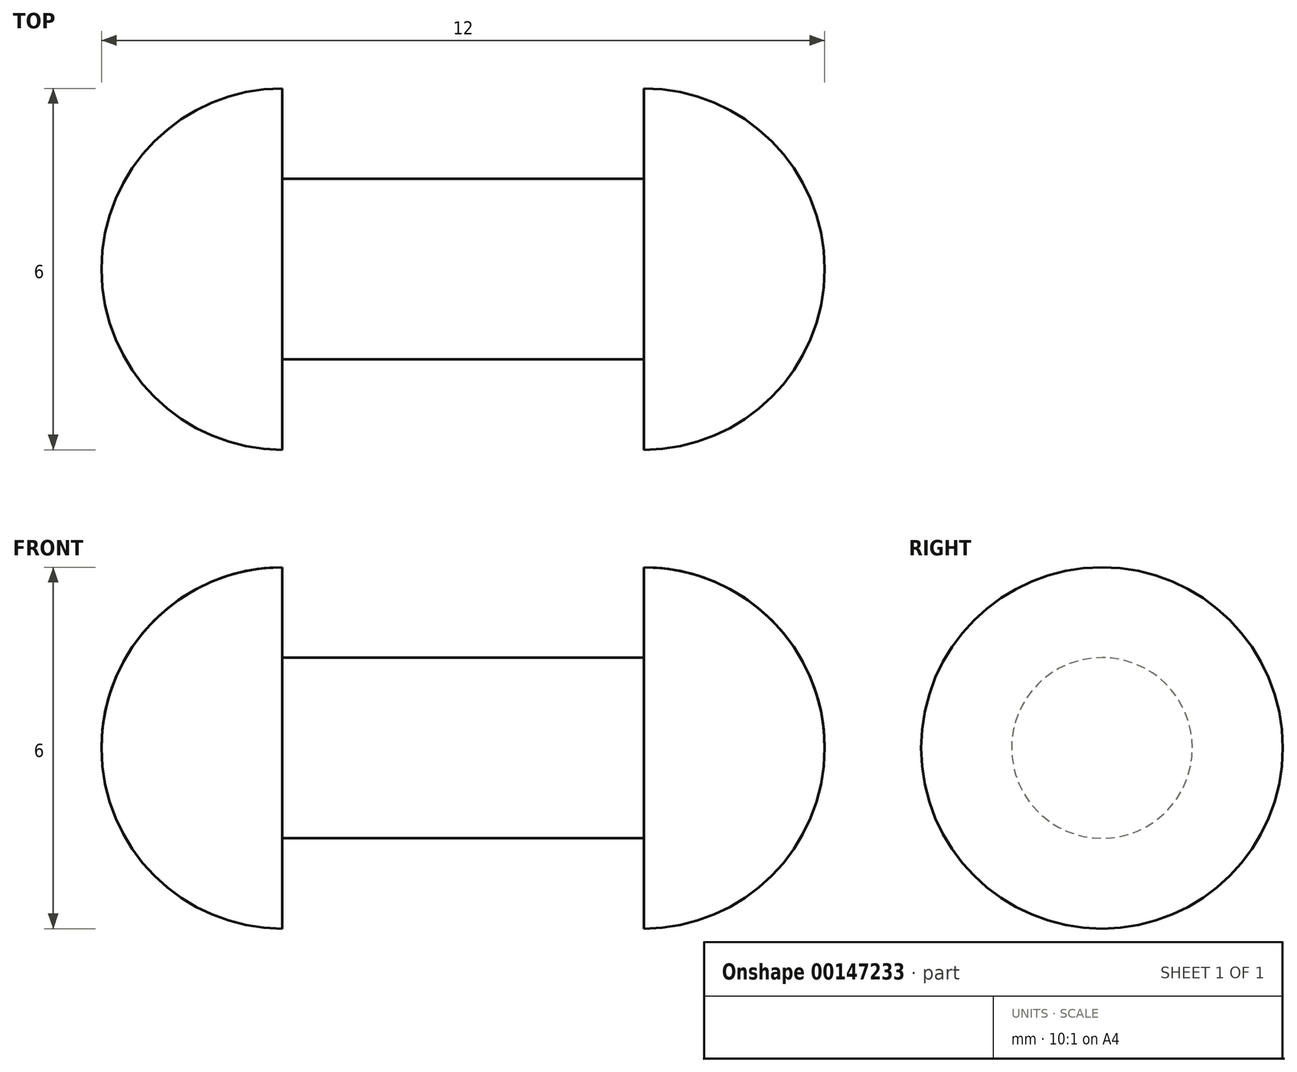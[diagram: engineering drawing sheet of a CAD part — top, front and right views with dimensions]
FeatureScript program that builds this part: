
annotation { "Feature Type Name" : "Feature", "Feature Type Description" : "" }
export const myFeature = defineFeature(function(context is Context, id is Id, definition is map)
    precondition{}
    {
        {
            var Q0;
            Q0=qCreatedBy(makeId("Front.planeOp"),FACE);
            var sketch = newSketch(context, id + "F0", { "sketchPlane" : qUnion([Q0])});
            skArc(sketch, "E0", {"start": v(0, 3) * mm, "mid": v(-2.12, 2.12) * mm, "end": v(-3, 0) * mm});
            skArc(sketch, "E1", {"start": v(9, 0) * mm, "mid": v(8.12, 2.12) * mm, "end": v(6, 3) * mm});
            skLineSegment(sketch, "E2", {"start": v(0, 3) * mm, "end": v(0, 1.5) * mm});
            skLineSegment(sketch, "E3", {"start": v(6, 3) * mm, "end": v(6, 1.5) * mm});
            skLineSegment(sketch, "E4", {"start": v(0, 1.5) * mm, "end": v(6, 1.5) * mm});
            skLineSegment(sketch, "E5", {"start": v(-3, 0) * mm, "end": v(9, 0) * mm});
            skPoint(sketch, "E6.trimOffspring.end.orphan", {"position": v(0, -3) * mm});
            skPoint(sketch, "E7.orphan", {"position": v(6, -3) * mm});
            skLineSegment(sketch, "E8", {"start": v(-3, 0) * mm, "end": v(-7.08, 0) * mm, "construction": true});
            skSolve(sketch);
        }
        {
            var Q0;
            Q0 = qSketchRegion(id + "F0", true);
            var Q1;
            Q1=sQuery(id+"F0.wireOp",EDGE,"E8");
            revolve(context, id + "F1", {"entities" : qUnion([Q0]), "axis" : qUnion([Q1]), "revolveType" : RevolveType.FULL});
        }
    });
